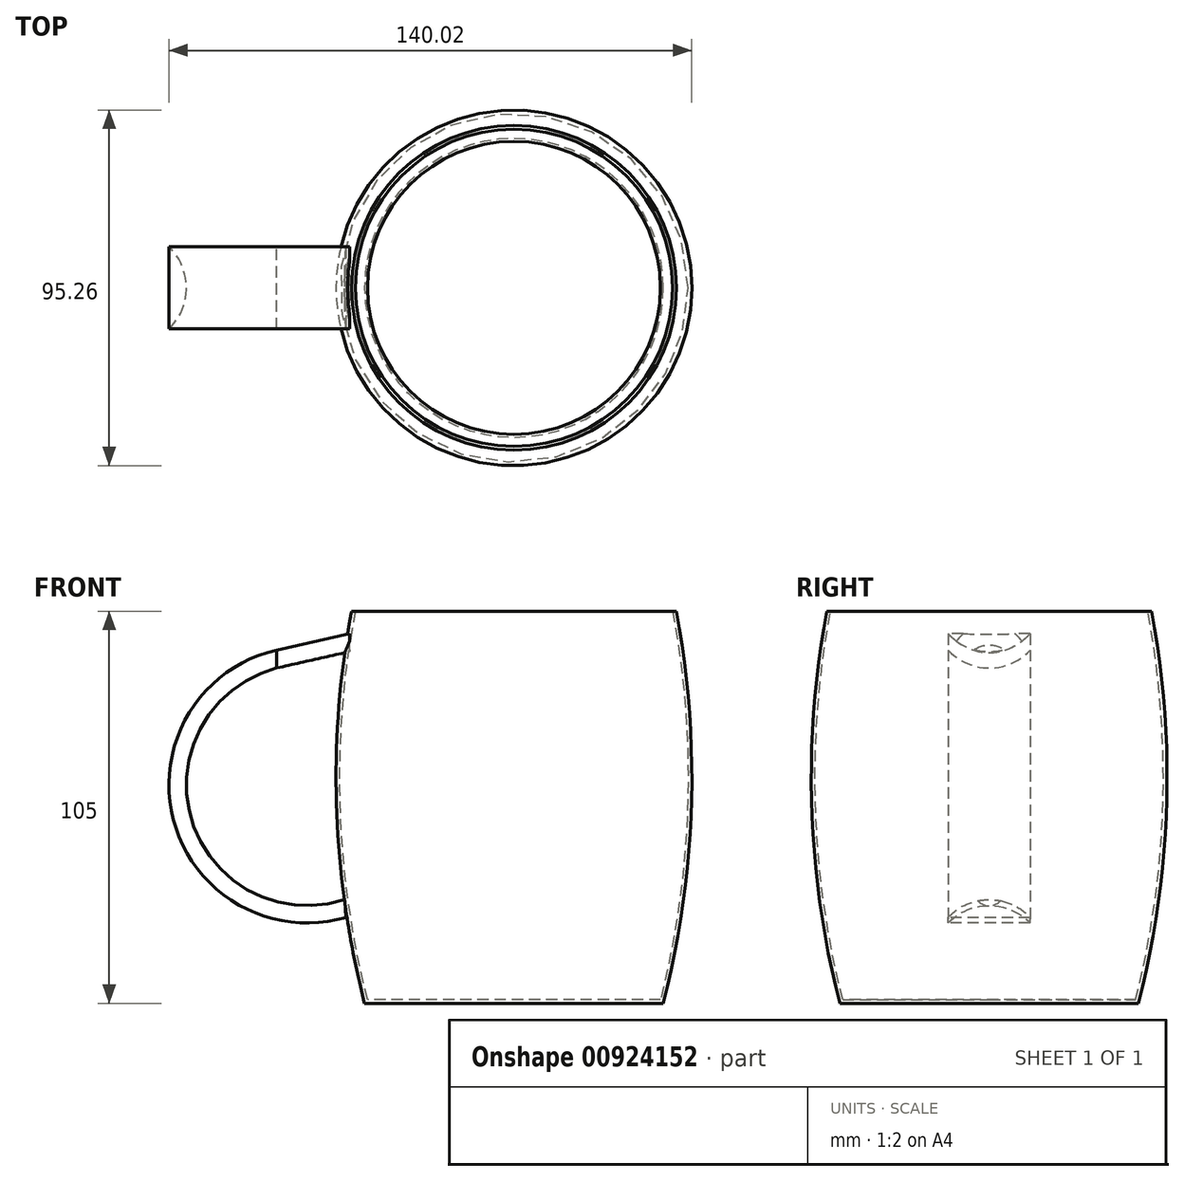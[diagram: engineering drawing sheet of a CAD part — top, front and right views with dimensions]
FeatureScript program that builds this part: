
annotation { "Feature Type Name" : "Feature", "Feature Type Description" : "" }
export const myFeature = defineFeature(function(context is Context, id is Id, definition is map)
    precondition{}
    {
        {
            var Q0;
            Q0=qCreatedBy(makeId("Front.planeOp"),FACE);
            var sketch = newSketch(context, id + "F0", { "sketchPlane" : qUnion([Q0])});
            skLineSegment(sketch, "E0", {"start": v(0, 52.5) * mm, "end": v(0, -52.5) * mm, "construction": true});
            skArc(sketch, "E1", {"start": v(-43.5, 52.5) * mm, "mid": v(-47.5, -0.2) * mm, "end": v(-40, -52.5) * mm});
            skPoint(sketch, "E2", {"position": v(-47.5, -0.2) * mm});
            skLineSegment(sketch, "E3", {"start": v(0, -52.5) * mm, "end": v(-40, -52.5) * mm});
            skArc(sketch, "E4.0", {"start": v(-42.48, 52.5) * mm, "mid": v(-46.52, 0.32) * mm, "end": v(-39.22, -51.5) * mm});
            skLineSegment(sketch, "E4.1", {"start": v(0, -51.5) * mm, "end": v(-39.22, -51.5) * mm});
            skLineSegment(sketch, "E5", {"start": v(-43.5, 52.5) * mm, "end": v(-42.48, 52.5) * mm});
            skLineSegment(sketch, "E6", {"start": v(0, -51.5) * mm, "end": v(0, -52.5) * mm});
            skSolve(sketch);
        }
        {
            var Q0;
            Q0=makeQuery(id+"F0.imprint","IMPRINT",FACE,{"disambiguationData":[TD([[makeQuery(id+"F0.imprint","IMPRINT",EDGE,{"derivedFrom":sQuery(id+"F0.wireOp",EDGE,"E1")}),1.0]])]});
            var Q1;
            Q1=sQuery(id+"F0.wireOp",EDGE,"E0");
            revolve(context, id + "F1", {"surfaceOperationType" : NewSurfaceOperationType.NEW, "entities" : qUnion([Q0]), "axis" : qUnion([Q1]), "revolveType" : RevolveType.FULL});
        }
        {
            var Q0;
            Q0=qCreatedBy(makeId("Front.planeOp"),FACE);
            var sketch = newSketch(context, id + "F2", { "sketchPlane" : qUnion([Q0])});
            skLineSegment(sketch, "E7", {"start": v(-44, 46.5) * mm, "end": v(-63.51, 42.1) * mm});
            skArc(sketch, "E8", {"start": v(-63.51, 42.1) * mm, "mid": v(-91.21, -3.25) * mm, "end": v(-45, -29.5) * mm});
            skPoint(sketch, "E9", {"position": v(-89.65, -7.97) * mm});
            skSolve(sketch);
        }
        {
            var Q0;
            Q0=qCreatedBy(makeId("Right.planeOp"),FACE);
            cPlane(context, id + "F3", {"entities" : qUnion([Q0]), "cplaneType" : CPlaneType.OFFSET, "offset" : 44 * mm, "oppositeDirection" : true, "width" : 150 * mm, "height" : 150 * mm});
        }
        {
            var Q0;
            Q0=qCreatedBy(id+"F3.planeOp",FACE);
            var sketch = newSketch(context, id + "F4", { "sketchPlane" : qUnion([Q0])});
            skLineSegment(sketch, "E10", {"start": v(11, 46.5) * mm, "end": v(-11, 46.5) * mm});
            skArc(sketch, "E11", {"start": v(-11, 46.5) * mm, "mid": v(0, 41.7) * mm, "end": v(11, 46.5) * mm});
            skSolve(sketch);
        }
        {
            var Q0;
            Q0=makeQuery(id+"F4.imprint","IMPRINT",FACE,{"disambiguationData":[TD([[makeQuery(id+"F4.imprint","IMPRINT",EDGE,{"derivedFrom":sQuery(id+"F4.wireOp",EDGE,"E10")}),1.0]])]});
            var Q1;
            Q1=sQuery(id+"F2.wireOp",EDGE,"E7");
            var Q2;
            Q2=sQuery(id+"F2.wireOp",EDGE,"E8");
            sweep(context, id + "F5", {"operationType" : NewBodyOperationType.ADD, "profiles" : qUnion([Q0]), "path" : qUnion([Q1, Q2])});
        }
    });
